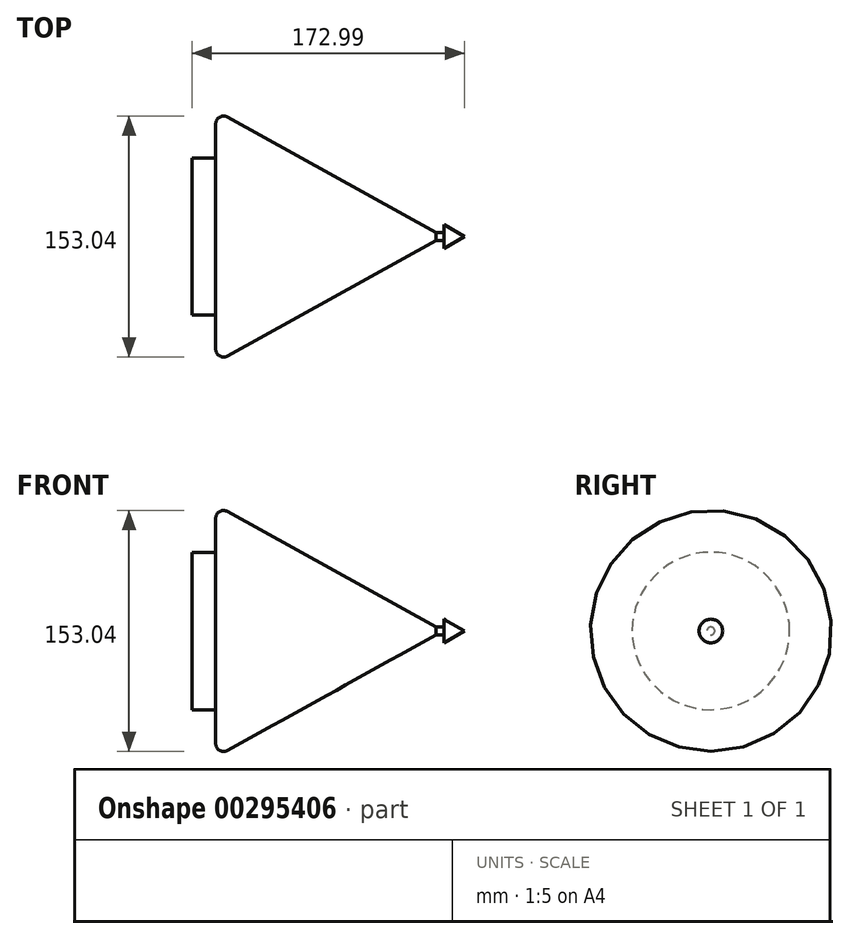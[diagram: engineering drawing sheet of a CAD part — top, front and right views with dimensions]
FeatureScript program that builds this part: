
annotation { "Feature Type Name" : "Feature", "Feature Type Description" : "" }
export const myFeature = defineFeature(function(context is Context, id is Id, definition is map)
    precondition{}
    {
        {
            var Q0;
            Q0=qCreatedBy(makeId("Front.planeOp"),FACE);
            var sketch = newSketch(context, id + "F0", { "sketchPlane" : qUnion([Q0])});
            skLineSegment(sketch, "E0", {"start": v(0, 0) * mm, "end": v(201.37, 0) * mm, "construction": true});
            skLineSegment(sketch, "E1", {"start": v(0, 0) * mm, "end": v(-52.08, 0) * mm, "construction": true});
            skLineSegment(sketch, "E2", {"start": v(0, 0) * mm, "end": v(0, 50) * mm});
            skLineSegment(sketch, "E3", {"start": v(0, 50) * mm, "end": v(15, 50) * mm});
            skLineSegment(sketch, "E4", {"start": v(15, 50) * mm, "end": v(15, 71.52) * mm});
            skLineSegment(sketch, "E5", {"start": v(22.42, 75.9) * mm, "end": v(155, 2.5) * mm});
            skLineSegment(sketch, "E6", {"start": v(155, 2.5) * mm, "end": v(160, 2.5) * mm});
            skLineSegment(sketch, "E7", {"start": v(160, 2.5) * mm, "end": v(160, 7.5) * mm});
            skLineSegment(sketch, "E8", {"start": v(160, 7.5) * mm, "end": v(173, 0) * mm});
            skPoint(sketch, "E9.visualSharp", {"position": v(15, 80) * mm});
            skArc(sketch, "E9.filletArc", {"start": v(22.42, 75.9) * mm, "mid": v(17.46, 75.82) * mm, "end": v(15, 71.52) * mm});
            skPoint(sketch, "E10.start.orphan", {"position": v(100, 2.5) * mm});
            skLineSegment(sketch, "E11", {"start": v(0, 0) * mm, "end": v(173, 0) * mm});
            skSolve(sketch);
        }
        {
            var Q0;
            Q0 = qSketchRegion(id + "F0", true);
            var Q1;
            Q1=sQuery(id+"F0.wireOp",EDGE,"E1");
            revolve(context, id + "F1", {"entities" : qUnion([Q0]), "axis" : qUnion([Q1]), "revolveType" : RevolveType.FULL});
        }
    });
